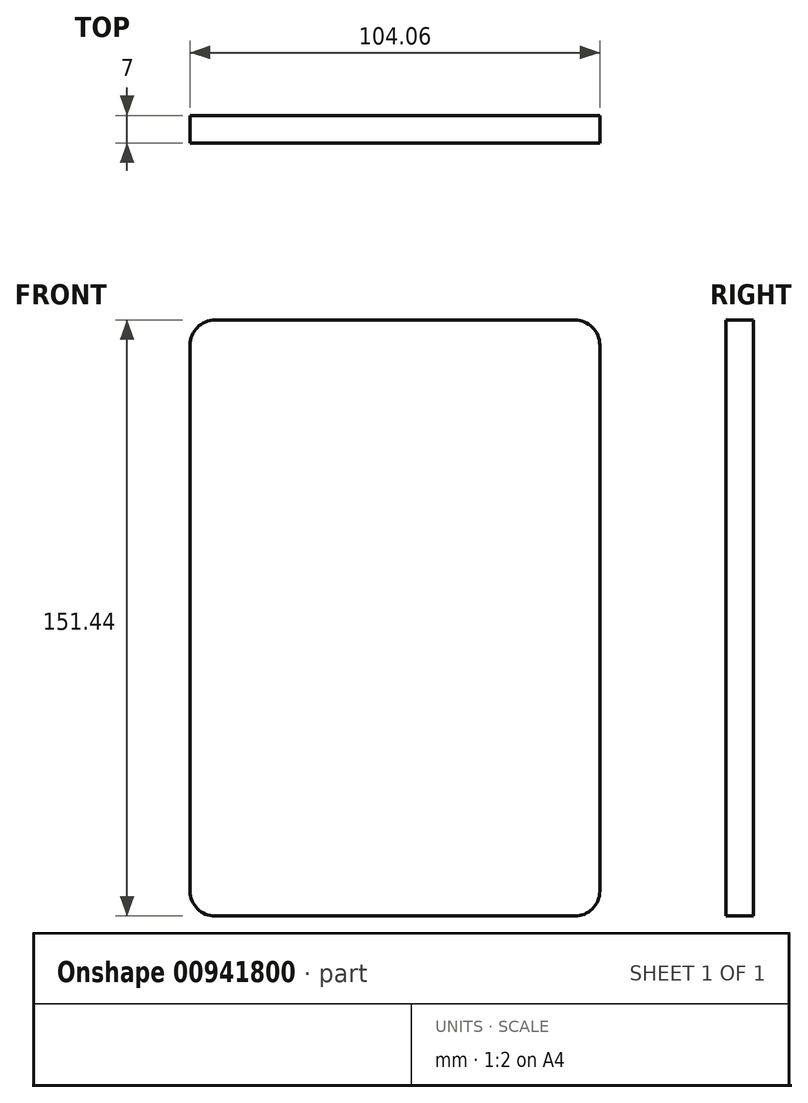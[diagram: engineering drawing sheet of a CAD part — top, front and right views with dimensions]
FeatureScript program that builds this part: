
annotation { "Feature Type Name" : "Feature", "Feature Type Description" : "" }
export const myFeature = defineFeature(function(context is Context, id is Id, definition is map)
    precondition{}
    {
        {
            var Q0;
            Q0=qCreatedBy(makeId("Front.planeOp"),FACE);
            var sketch = newSketch(context, id + "F0", { "sketchPlane" : qUnion([Q0])});
            skLineSegment(sketch, "E0.bottom", {"start": v(-45.68, 75.72) * mm, "end": v(45.68, 75.72) * mm});
            skLineSegment(sketch, "E0.top", {"start": v(-45.68, -75.72) * mm, "end": v(45.68, -75.72) * mm});
            skLineSegment(sketch, "E0.left", {"start": v(-52.03, 69.37) * mm, "end": v(-52.03, -69.37) * mm});
            skLineSegment(sketch, "E0.right", {"start": v(52.03, 69.37) * mm, "end": v(52.03, -69.37) * mm});
            skPoint(sketch, "E0.middle", {"position": v(0, 0) * mm});
            skPoint(sketch, "E1.visualSharp", {"position": v(52.03, 75.72) * mm});
            skArc(sketch, "E1.filletArc", {"start": v(52.03, 69.37) * mm, "mid": v(50.17, 73.86) * mm, "end": v(45.68, 75.72) * mm});
            skPoint(sketch, "E2.visualSharp", {"position": v(52.03, -75.72) * mm});
            skArc(sketch, "E2.filletArc", {"start": v(45.68, -75.72) * mm, "mid": v(50.17, -73.86) * mm, "end": v(52.03, -69.37) * mm});
            skPoint(sketch, "E3.visualSharp", {"position": v(-52.03, -75.72) * mm});
            skArc(sketch, "E3.filletArc", {"start": v(-52.03, -69.37) * mm, "mid": v(-50.17, -73.86) * mm, "end": v(-45.68, -75.72) * mm});
            skPoint(sketch, "E4.visualSharp", {"position": v(-52.03, 75.72) * mm});
            skArc(sketch, "E4.filletArc", {"start": v(-45.68, 75.72) * mm, "mid": v(-50.17, 73.86) * mm, "end": v(-52.03, 69.37) * mm});
            skSolve(sketch);
        }
        {
            var Q0;
            Q0=makeQuery(id+"F0.imprint","IMPRINT",FACE,{"disambiguationData":[TD([[makeQuery(id+"F0.imprint","IMPRINT",EDGE,{"derivedFrom":sQuery(id+"F0.wireOp",EDGE,"E0.bottom")}),-1.0]])]});
            extrude(context, id + "F1", {"entities" : qUnion([Q0]), "endBound" : BoundingType.SYMMETRIC, "depth" : 7 * mm, "offsetDistance" : 25.4 * mm});
        }
    });
